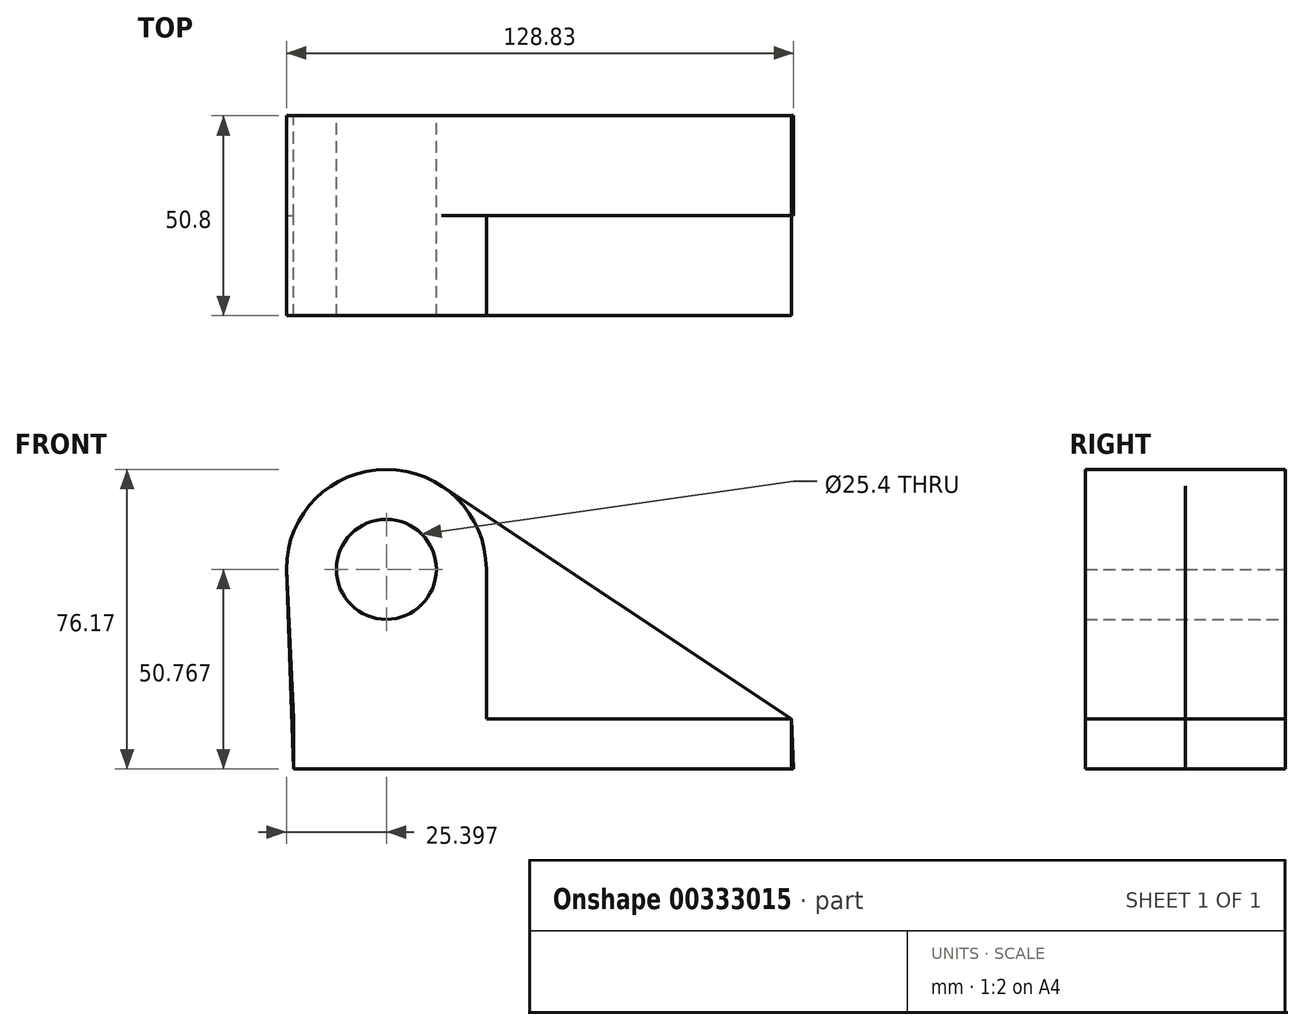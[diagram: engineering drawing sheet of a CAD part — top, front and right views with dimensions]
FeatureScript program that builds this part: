
annotation { "Feature Type Name" : "Feature", "Feature Type Description" : "" }
export const myFeature = defineFeature(function(context is Context, id is Id, definition is map)
    precondition{}
    {
        {
            var Q0;
            Q0=qCreatedBy(makeId("Front.planeOp"),FACE);
            var sketch = newSketch(context, id + "F0", { "sketchPlane" : qUnion([Q0])});
            skCircle(sketch, "E0", {"center": v(-38.47, 50.77) * mm, "radius": 12.7 * mm});
            skCircle(sketch, "E1", {"center": v(-38.47, 50.77) * mm, "radius": 25.4 * mm});
            skLineSegment(sketch, "E2", {"start": v(-38.47, 50.77) * mm, "end": v(-63.87, 50.77) * mm});
            skLineSegment(sketch, "E3", {"start": v(-63.87, 50.77) * mm, "end": v(-62.04, 0) * mm});
            skLineSegment(sketch, "E4", {"start": v(-62.04, 0) * mm, "end": v(64.96, 0) * mm});
            skLineSegment(sketch, "E5", {"start": v(64.96, 0) * mm, "end": v(64.5, 12.7) * mm});
            skLineSegment(sketch, "E6", {"start": v(64.5, 12.7) * mm, "end": v(-24.4, 71.9) * mm});
            skSolve(sketch);
        }
        {
            var Q0;
            Q0=makeQuery(id+"F0.imprint","IMPRINT",FACE,{"disambiguationData":[TD([[makeQuery(id+"F0.imprint","IMPRINT",EDGE,{"derivedFrom":sQuery(id+"F0.wireOp",EDGE,"E0")}),-1.0]])]});
            var Q1;
            {var subQ0=sQuery(id+"F0.wireOp",EDGE,"E4");Q1=makeQuery(id+"F0.imprint","IMPRINT",FACE,{"disambiguationData":[TD([[makeQuery(id+"F0.imprint","IMPRINT",EDGE,{"derivedFrom":subQ0}),1.0]])]});}
            extrude(context, id + "F1", {"entities" : qUnion([Q0, Q1]), "depth" : 25.4 * mm});
        }
        {
            var Q0;
            Q0=makeQuery(id+"F1.opExtrude","CAP_FACE",FACE,{"disambiguationData":[OSD([sQuery(id+"F0.wireOp",EDGE,"E0"),sQuery(id+"F0.wireOp",EDGE,"E1"),sQuery(id+"F0.wireOp",EDGE,"E3"),sQuery(id+"F0.wireOp",EDGE,"E4"),sQuery(id+"F0.wireOp",EDGE,"E5"),sQuery(id+"F0.wireOp",EDGE,"E6")])],"isStart":false});
            var sketch = newSketch(context, id + "F2", { "sketchPlane" : qUnion([Q0])});
            skCircle(sketch, "E7", {"center": v(-38.47, 50.77) * mm, "radius": 12.7 * mm});
            skArc(sketch, "E8", {"start": v(-13.07, 50.77) * mm, "mid": v(-39.7, 76.14) * mm, "end": v(-63.76, 48.33) * mm});
            skLineSegment(sketch, "E9.bottom", {"start": v(64.5, 12.7) * mm, "end": v(-13.07, 12.7) * mm});
            skLineSegment(sketch, "E9.top", {"start": v(64.5, 0) * mm, "end": v(-62.04, 0) * mm});
            skLineSegment(sketch, "E9.left", {"start": v(64.5, 12.7) * mm, "end": v(64.5, 0) * mm});
            skLineSegment(sketch, "E9.right", {"start": v(-62.04, 12.7) * mm, "end": v(-62.04, 0) * mm});
            skLineSegment(sketch, "E10", {"start": v(-63.87, 50.77) * mm, "end": v(-62.04, 12.7) * mm});
            skLineSegment(sketch, "E11", {"start": v(-13.07, 50.77) * mm, "end": v(-13.07, 12.7) * mm});
            skSolve(sketch);
        }
        {
            var Q0;
            Q0=makeQuery(id+"F2.imprint","IMPRINT",FACE,{"disambiguationData":[TD([[makeQuery(id+"F2.imprint","IMPRINT",EDGE,{"derivedFrom":sQuery(id+"F2.wireOp",EDGE,"E7")}),-1.0]])]});
            extrude(context, id + "F3", {"entities" : qUnion([Q0]), "operationType" : NewBodyOperationType.ADD, "depth" : 25.4 * mm});
        }
    });
